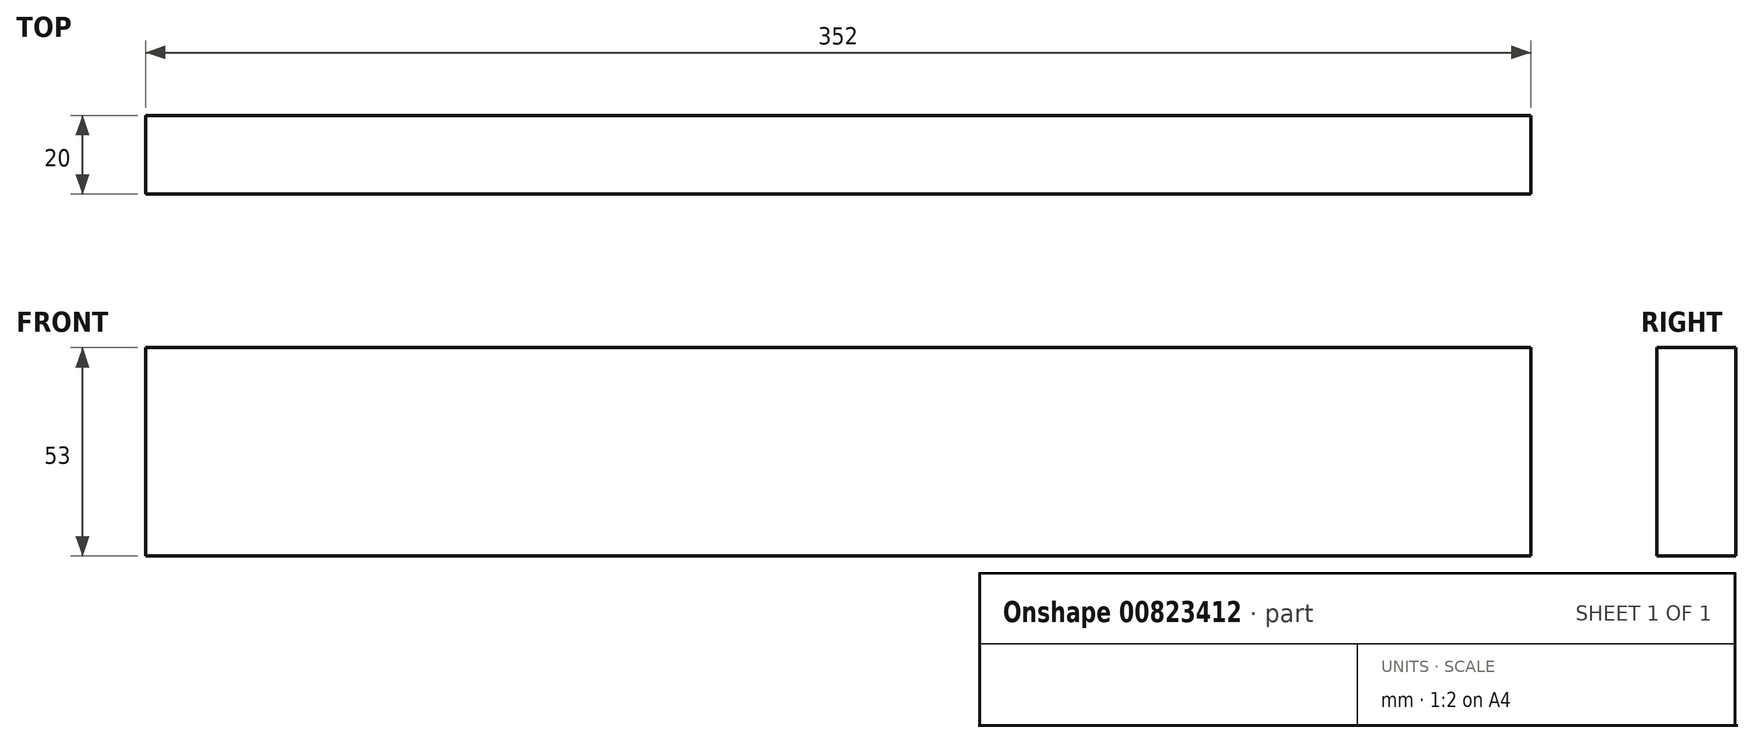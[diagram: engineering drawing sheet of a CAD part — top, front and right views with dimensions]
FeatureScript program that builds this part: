
annotation { "Feature Type Name" : "Feature", "Feature Type Description" : "" }
export const myFeature = defineFeature(function(context is Context, id is Id, definition is map)
    precondition{}
    {
        {
            var Q0;
            Q0=qCreatedBy(makeId("Front.planeOp"),FACE);
            var sketch = newSketch(context, id + "F0", { "sketchPlane" : qUnion([Q0])});
            skLineSegment(sketch, "E0.bottom", {"start": v(-176, 26.5) * mm, "end": v(176, 26.5) * mm});
            skLineSegment(sketch, "E0.top", {"start": v(-176, -26.5) * mm, "end": v(176, -26.5) * mm});
            skLineSegment(sketch, "E0.left", {"start": v(-176, 26.5) * mm, "end": v(-176, -26.5) * mm});
            skLineSegment(sketch, "E0.right", {"start": v(176, 26.5) * mm, "end": v(176, -26.5) * mm});
            skPoint(sketch, "E0.middle", {"position": v(0, 0) * mm});
            skSolve(sketch);
        }
        {
            var Q0;
            Q0 = qSketchRegion(id + "F0", true);
            extrude(context, id + "F1", {"entities" : qUnion([Q0]), "endBound" : BoundingType.SYMMETRIC, "depth" : 20 * mm, "offsetDistance" : 25 * mm});
        }
    });
